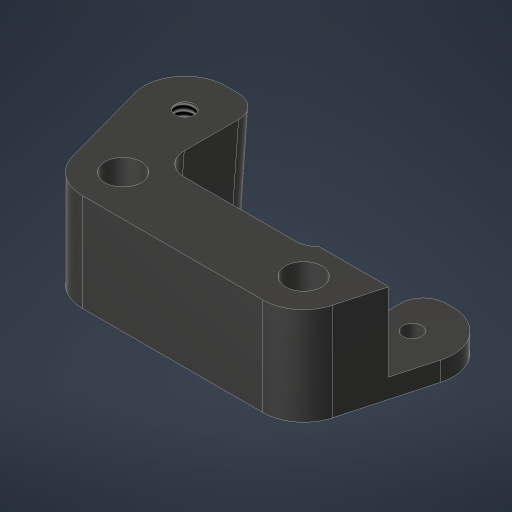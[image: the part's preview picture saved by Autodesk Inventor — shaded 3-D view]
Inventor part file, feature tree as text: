
AUTODESK INVENTOR PART (.ipt)
format: ipt  version: 2023.4 (Build 274418000, 418)  size: 267,264 bytes
history: native  units: in
note: dims shown in document units (in); Inventor stores cm internally (conversion verified against a paired STEP export)
features: sketch x5, extrude x4, hole x2, fillet x2, projected_geometry x1
ambient origin geometry x8: Origin, YZ Plane, XZ Plane, XY Plane, X Axis, Y Axis, Z Axis, Center Point
bodies: Solid1 (feature_tree)
feature tree (14):
  sketch  "Sketch1"  dims[d0=1.13in d1=1.0in]
  sketch  "Sketch2"  dims[d2=1.375in d3=1.75in]
  extrude  "Extrusion1"  Depth=1.0in
  hole  "Hole1"  [1 undecoded]
  hole  "Hole2"  [1 undecoded]
  sketch  "Sketch3"  dims[d4=2.5in d5=2.3622in d7=360.0deg]
  extrude  "Extrusion3"  Depth=1.2773in
  fillet  "Fillet2"  Radius=1.2773in
  extrude  "Extrusion4"  Depth=0.5118in
  extrude  "Extrusion2"  Depth=0.5118in
  fillet  "Fillet1"  Radius=4.2441in
  sketch  "Sketch4"  dims[d9=0.375in d10=1.2773in d11=1.2773in]
  sketch  "Sketch5"  dims[d12=0.201in d14=0.0237in d15=1.2598in d16=4.2441in d18=1.6in d19=0.201in d20=0.275in d21=0.201in d22=0.201in d23=0.125in d24=0.54in d25=0.0in d26=0.201in d27=0.38in d28=0.385in d29=0.25in d30=0.5635in d31=1.0in d32=0.8108in d33=0.104in d34=0.276in d35=0.375in d36=0.25in d37=0.5635in d38=1.0in d39=0.8108in d40=0.9449in d41=0.6106in d42=0.0in d43=0.0in d44=0.125in d45=0.8661in d46=0.8661in d47=0.9449in d48=0.5512in d49=0.0in d50=0.125in d53=1.0in d54=0.0in d55=0.4331in d56=0.5118in]
  projected_geometry  "Project Cut Edges1"
note: 2 required parameter values undecoded (feature->parameter linkage not recoverable at this tier; creation-order binding heuristic only, values carry confidence <= 0.55)
